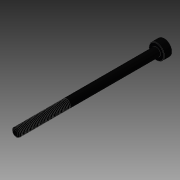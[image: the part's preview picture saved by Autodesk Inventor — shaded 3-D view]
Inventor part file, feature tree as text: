
AUTODESK INVENTOR PART (.ipt)
format: ipt  version: 2015 (Build 190159000, 159)  size: 1,564,160 bytes
history: native  units: in
note: dims shown in document units (in); Inventor stores cm internally (conversion verified against a paired STEP export)
features: revolve x1, other x1, imported_body x1
ambient origin geometry x8: Origin, YZ Plane, XZ Plane, XY Plane, X Axis, Y Axis, Z Axis, Center Point
bodies: Body1 (feature_tree)
feature tree (3):
  revolve  "Revolve1"  [1 undecoded]
  other  "91290A1371"
  imported_body  "Base1"
note: 1 required parameter value undecoded (feature->parameter linkage not recoverable at this tier; creation-order binding heuristic only, values carry confidence <= 0.55)
